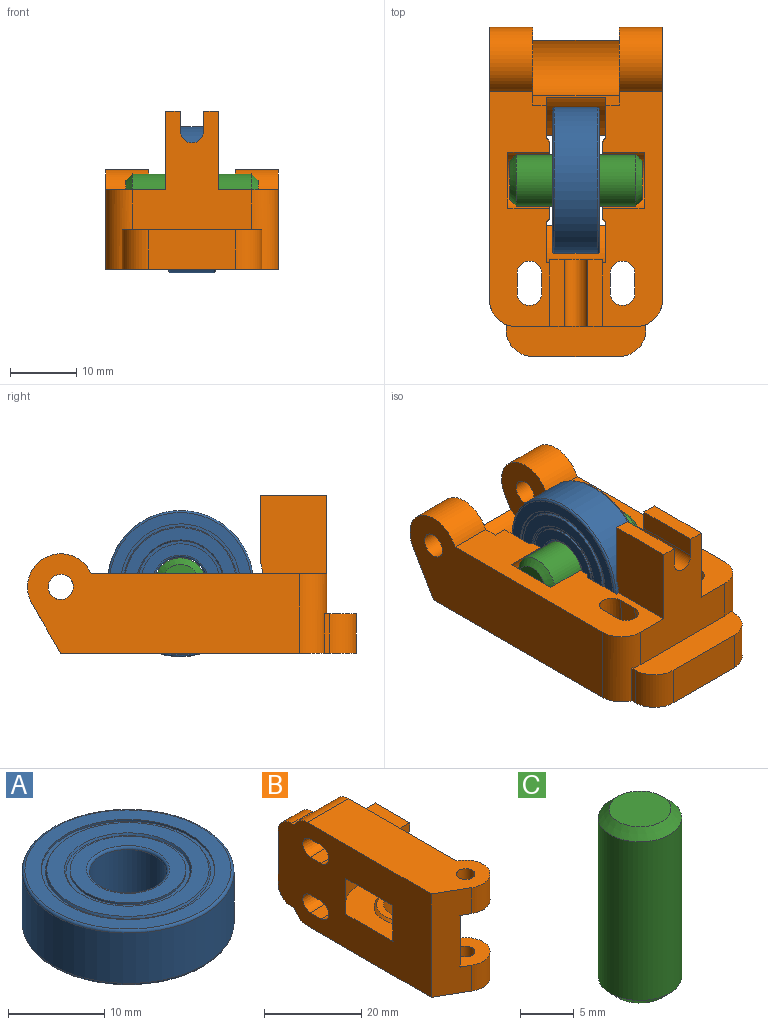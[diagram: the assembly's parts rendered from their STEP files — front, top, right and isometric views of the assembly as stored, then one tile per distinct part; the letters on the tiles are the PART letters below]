
ASSEMBLY  parts=3 mates=2
PART A: 25 faces, bbox 23.8x23.8x7 mm
  f0: cylinder r=4mm len=8mm, axis (0,0,-1), area 160.8mm2, adj f20,f23
  f1: plane 12x12mm, normal (0,0,-1), area 55mm2, adj f2,f20
  f2: cylinder r=6mm len=12mm, axis (0,0,-1), area 9.4mm2, adj f1,f3
  f3: plane 12.88x12.88mm, normal (0,0,-1), area 17.1mm2, adj f2,f4
  f4: cone r=6.44mm half-angle=30deg, axis (0,0,-1), area 11.8mm2, adj f3,f5
  f5: plane 16.84x16.84mm, normal (0,0,-1), area 86.5mm2, adj f4,f6
  f6: cone r=8.42mm half-angle=30deg, axis (0,0,1), area 15.4mm2, adj f5,f7
  f7: plane 18x18mm, normal (0,0,-1), area 24.1mm2, adj f6,f8
  f8: cylinder r=9mm len=18mm, axis (0,0,-1), area 14.1mm2, adj f7,f9
  f9: plane 21.4x21.4mm, normal (0,0,-1), area 105.2mm2, adj f8,f21
  f10: cylinder r=11mm len=22mm, axis (0,0,-1), area 442.3mm2, adj f21,f22
  f11: plane 21.4x21.4mm, normal (0,0,1), area 105.2mm2, adj f12,f22
  f12: cylinder r=9mm len=18mm, axis (0,0,-1), area 14.1mm2, adj f11,f13
  f13: plane 18x18mm, normal (0,0,1), area 24.1mm2, adj f12,f14
  f14: cone r=8.42mm half-angle=30deg, axis (0,0,-1), area 15.4mm2, adj f13,f15
  f15: plane 16.84x16.84mm, normal (0,0,1), area 86.5mm2, adj f14,f16
  f16: cone r=6.44mm half-angle=30deg, axis (0,0,1), area 11.8mm2, adj f15,f17
  f17: plane 12.88x12.88mm, normal (0,0,1), area 17.1mm2, adj f16,f18
  f18: cylinder r=6mm len=12mm, axis (0,0,-1), area 9.4mm2, adj f17,f19
  f19: plane 12x12mm, normal (0,0,1), area 55mm2, adj f18,f23
  f20: torus R=4.3mm, axis (0,0,-1), area 12.2mm2, adj f0,f1
  f21: torus R=10.7mm, axis (0,0,-1), area 32.2mm2, adj f9,f10
  f22: torus R=10.7mm, axis (0,0,-1), area 32.2mm2, adj f10,f11
  f23: torus R=4.3mm, axis (0,0,-1), area 12.2mm2, adj f0,f19
  f24: torus R=7.5mm, axis (0,0,-1), area 647.7mm2
PART B: 51 faces, bbox 23.8x49.5x26 mm
  f0: plane 24.91x12mm, normal (0,0,-1), area 178.1mm2, adj f1,f2,f3,f40,f41,f49
  f1: plane 35.42x9.06mm, normal (1,0,0), area 230.1mm2, adj f0,f3,f6,f7,f13,f15,f21,f26
  f2: plane 44.5x26mm, normal (-1,0,0), area 939.4mm2, adj f0,f8,f12,f13,f17,f18,f19,f21
  f3: plane 13x3.92mm, normal (0.34,-0.94,0), area 25.3mm2, adj f0,f1,f4,f14,f15,f16,f41,f42
  f4: plane 35.42x9.06mm, normal (1,0,0), area 230.1mm2, adj f3,f6,f10,f12,f16,f22,f25,f36
  f5: plane 10x2.25mm, normal (1,0,0), area 22.5mm2, adj f6,f26,f27,f31
  f6: plane 18x17.8mm, normal (0,1,0), area 187.1mm2, adj f1,f4,f5,f20,f21,f22,f25,f26
  f7: cylinder r=5mm len=9.58mm, axis (0,0,1), area 105.7mm2, adj f1,f8,f13,f15
  f8: plane 26x7.5mm, normal (-0.5,-0.87,0), area 192.4mm2, adj f2,f7,f10,f12,f13,f14,f15,f16
  f9: cylinder r=1.9mm len=6.5mm, axis (0,0,1), area 77.6mm2, adj f13,f15
  f10: cylinder r=5mm len=9.58mm, axis (0,0,1), area 105.7mm2, adj f4,f8,f12,f16
  f11: cylinder r=1.9mm len=6.5mm, axis (0,0,1), area 77.6mm2, adj f12,f16
  f12: plane 41x15mm, normal (0,0,-1), area 478.4mm2, adj f2,f4,f8,f10,f11,f22
  f13: plane 41x15mm, normal (0,0,1), area 478.4mm2, adj f1,f2,f7,f8,f9,f21
  f14: cylinder r=5.6mm len=13mm, axis (0,0,-1), area 131.2mm2, adj f3,f8,f15,f16
  f15: plane 11.69x10.6mm, normal (0,0,-1), area 77.7mm2, adj f1,f3,f7,f8,f9,f14
  f16: plane 11.69x10.6mm, normal (0,0,1), area 77.7mm2, adj f3,f4,f8,f10,f11,f14
  f17: plane 6x0.79mm, normal (0,0,1), area 4.8mm2, adj f2,f20,f21,f23
  f18: plane 13x6mm, normal (0,1,0), area 78mm2, adj f2,f20,f23,f24
  f19: plane 6x0.79mm, normal (0,0,-1), area 4.8mm2, adj f2,f20,f22,f24
  f20: plane 21x4.79mm, normal (1,0,0), area 87.9mm2, adj f6,f17,f18,f19,f21,f22,f23,f24
  f21: cylinder r=4mm len=12mm, axis (1,0,0), area 66.2mm2, adj f1,f2,f6,f13,f17,f20
  f22: cylinder r=4mm len=12mm, axis (-1,0,0), area 66.2mm2, adj f2,f4,f6,f12,f19,f20
  f23: cylinder r=4mm len=6mm, axis (-1,0,0), area 37.7mm2, adj f2,f17,f18,f20
  f24: cylinder r=4mm len=6mm, axis (-1,0,0), area 37.7mm2, adj f2,f18,f19,f20
  f25: plane 11.8x10mm, normal (0,0,-1), area 117.5mm2, adj f4,f6,f27,f28,f40
  f26: plane 11.8x10mm, normal (0,0,1), area 117.5mm2, adj f1,f5,f6,f27,f40
  f27: plane 9.8x8mm, normal (0,-1,0), area 63.1mm2, adj f5,f25,f26,f28,f29,f30,f31,f40
  f28: plane 10x2.25mm, normal (1,0,0), area 22.5mm2, adj f6,f25,f27,f29
  f29: plane 10x3mm, normal (0,0,1), area 30mm2, adj f6,f27,f28,f30
  f30: cylinder r=1.75mm len=10mm, axis (0,1,0), area 55mm2, adj f6,f27,f29,f31
  f31: plane 10x3mm, normal (0,0,-1), area 30mm2, adj f5,f6,f27,f30
  f32: cone r=1.85mm half-angle=2deg, axis (-1,0,0), area 77.7mm2, adj f1,f2,f33,f35
  f33: plane 12x3mm, normal (-0.03,0,1), area 36mm2, adj f1,f2,f32,f34
  f34: cone r=1.85mm half-angle=2deg, axis (-1,0,0), area 77.7mm2, adj f1,f2,f33,f35
  f35: plane 12x3mm, normal (-0.03,0,-1), area 36mm2, adj f1,f2,f32,f34
  f36: plane 12x3mm, normal (-0.03,0,-1), area 36mm2, adj f2,f4,f37,f38
  f37: cone r=1.85mm half-angle=2deg, axis (-1,0,0), area 77.7mm2, adj f2,f4,f36,f39
  f38: cone r=1.85mm half-angle=2deg, axis (-1,0,0), area 77.7mm2, adj f2,f4,f36,f39
  f39: plane 12x3mm, normal (-0.03,0,1), area 36mm2, adj f2,f4,f37,f38
  f40: cylinder r=12.5mm len=14mm, axis (0,0,-1), area 142.1mm2, adj f0,f1,f2,f4,f25,f26,f27,f42
  f41: cylinder r=12.5mm len=9mm, axis (0,0,-1), area 98.6mm2, adj f0,f2,f3,f42
  f42: plane 24.91x12mm, normal (0,0,1), area 178.1mm2, adj f2,f3,f4,f40,f41,f50
  f43: cylinder r=4.45mm len=8.9mm, axis (0,0,-1), area 107.4mm2, adj f4,f44,f48
  f44: plane 8.9x5.95mm, normal (0,0,1), area 44.2mm2, adj f4,f43
  f45: cylinder r=4.45mm len=8.9mm, axis (0,0,-1), area 107.4mm2, adj f1,f46,f47
  f46: plane 8.9x5.95mm, normal (0,0,-1), area 44.2mm2, adj f1,f45
  f47: plane 11.8x7.4mm, normal (0,0,-1), area 28mm2, adj f1,f45,f49
  f48: plane 11.8x7.4mm, normal (0,0,1), area 28mm2, adj f4,f43,f50
  f49: cone r=5.9mm half-angle=45deg, axis (0,0,1), area 17.4mm2, adj f0,f1,f47
  f50: cone r=6.45mm half-angle=45deg, axis (0,0,-1), area 17.4mm2, adj f4,f42,f48
PART C: 5 faces, bbox 7.8x7.8x20 mm
  f0: cylinder r=3.88mm len=18mm, axis (0,0,1), area 438.3mm2, adj f3,f4
  f1: plane 5.75x5.75mm, normal (0,0,-1), area 26mm2, adj f3
  f2: plane 5.75x5.75mm, normal (0,0,1), area 26mm2, adj f4
  f3: cone r=2.88mm half-angle=45deg, axis (0,0,1), area 30mm2, adj f0,f1
  f4: cone r=3.88mm half-angle=45deg, axis (0,0,-1), area 30mm2, adj f0,f2
PLACE A rot(axis=(-0.58,0.58,-0.58),120deg) t=(0,3.34,10.5)mm
PLACE B rot(axis=(0.71,0,0.71),180deg) t=(-18.81,-14.66,63.05)mm
PLACE C rot(axis=(0,-1,0),90deg) t=(18.81,21.34,63.05)mm
MATE fastened C.f0 <-> A.f0  axis (-1,0,0) through (0,3.34,10.5)mm
MATE revolute C.f0 <-> B.f40  axis (-1,0,0) through (0,3.34,10.5)mm
